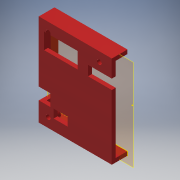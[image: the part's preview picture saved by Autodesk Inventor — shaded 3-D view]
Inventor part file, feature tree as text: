
AUTODESK INVENTOR PART (.ipt)
format: ipt  version: 2017 (Build 210142000, 142)  size: 244,224 bytes
history: native  units: in
note: dims shown in document units (in); Inventor stores cm internally (conversion verified against a paired STEP export)
features: reference x28, sketch x4, other x4, extrude x3, plane x1
ambient origin geometry x8: Origin, YZ Plane, XZ Plane, XY Plane, X Axis, Y Axis, Z Axis, Center Point
bodies: Solid1 (feature_tree)
feature tree (40):
  plane  "Work Plane1"
  extrude  "Extrusion1"  Depth=0.2in
  extrude  "Extrusion2"  Depth=0.03in
  extrude  "Extrusion3"  Depth=0.03in
  sketch  "Sketch4"  dims[d8=0.03in d9=0.03in d10=0.03in d11=0.03in d12=0.03in d17=0.115in d18=0.115in d19=0.115in d20=0.1in d21=0.0in d22=0.1in d23=0.1in d24=0.1in d25=0.1in d26=0.3in d27=0.0in d28=0.03in d29=0.03in d30=0.03in d31=0.03in d32=0.05in d33=0.015in]
  sketch  "Sketch1"  dims[d1=0.2in d2=0.0in d3=0.03in]
  reference  "Reference1"
  sketch  "Sketch2"  dims[d4=0.03in d5=0.03in]
  reference  "Reference2"
  reference  "Reference3"
  reference  "Reference4"
  reference  "Reference5"
  reference  "Reference6"
  reference  "Reference7"
  reference  "Reference8"
  reference  "Reference9"
  reference  "Reference10"
  reference  "Reference11"
  reference  "Reference12"
  reference  "Reference13"
  reference  "Reference14"
  reference  "Reference15"
  reference  "Reference16"
  reference  "Reference17"
  reference  "Reference18"
  reference  "Reference19"
  reference  "Reference20"
  reference  "Reference21"
  reference  "Reference22"
  reference  "Reference23"
  reference  "Reference24"
  sketch  "Sketch3"  dims[d6=0.03in d7=0.03in]
  reference  "Reference25"
  reference  "Reference26"
  reference  "Reference27"
  reference  "Reference28"
  other  "<userpath>\Documents\Inventor\PixyCam and Gimbal\Assembly2.iam"
  other  "Assembly2.iam"
  other  "PixyCamKinda:1"
  other  "Assembly1"
